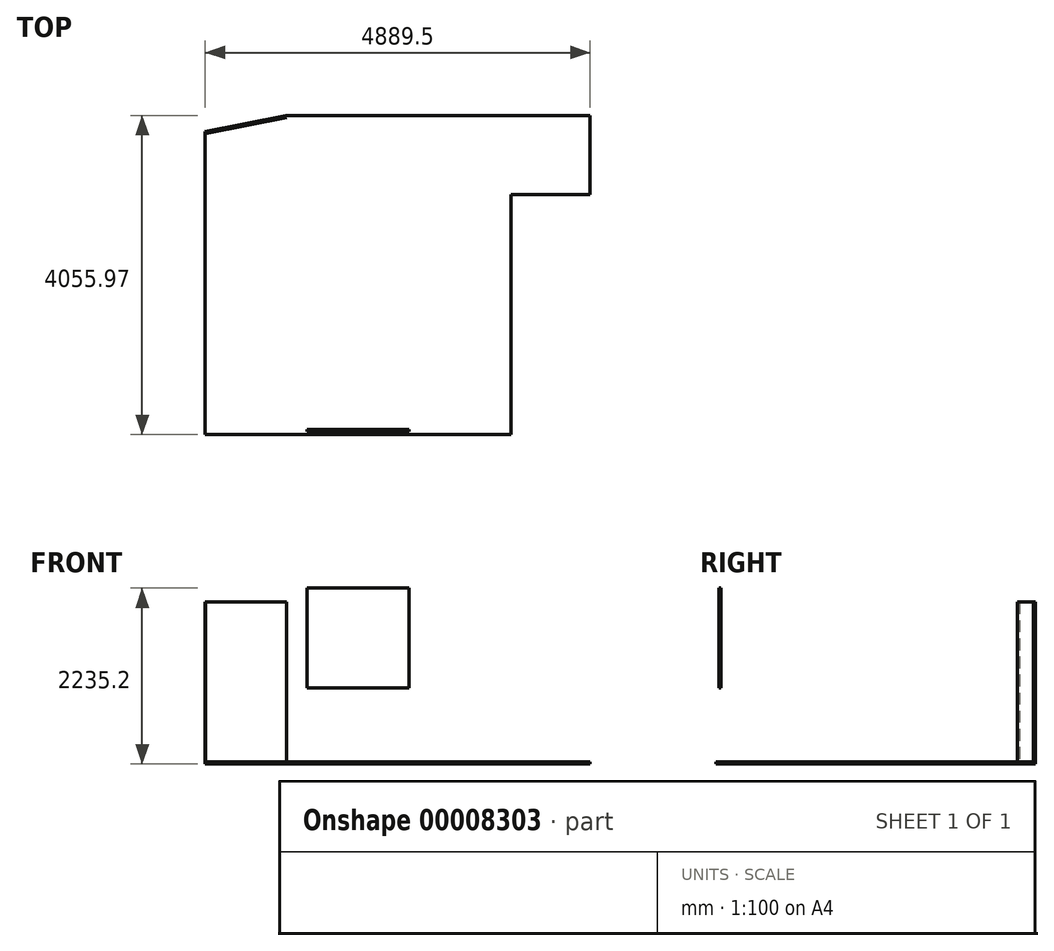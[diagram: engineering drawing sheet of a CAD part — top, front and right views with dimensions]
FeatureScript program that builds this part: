
annotation { "Feature Type Name" : "Feature", "Feature Type Description" : "" }
export const myFeature = defineFeature(function(context is Context, id is Id, definition is map)
    precondition{}
    {
        {
            var Q0;
            Q0=qCreatedBy(makeId("Top.planeOp"),FACE);
            var sketch = newSketch(context, id + "F0", { "sketchPlane" : qUnion([Q0])});
            skLineSegment(sketch, "E0", {"start": v(-541.3, 4018.52) * mm, "end": v(3319.5, 4018.52) * mm});
            skLineSegment(sketch, "E1", {"start": v(3319.5, 4018.52) * mm, "end": v(3319.5, 3015.22) * mm});
            skLineSegment(sketch, "E2", {"start": v(3319.5, 3015.22) * mm, "end": v(2316.2, 3015.22) * mm});
            skLineSegment(sketch, "E3", {"start": v(2316.2, 3015.22) * mm, "end": v(2316.2, -32.78) * mm});
            skLineSegment(sketch, "E4", {"start": v(2316.2, -32.78) * mm, "end": v(1020.8, -32.78) * mm});
            skLineSegment(sketch, "E5", {"start": v(1020.8, -32.78) * mm, "end": v(1020.8, -37.45) * mm});
            skLineSegment(sketch, "E6", {"start": v(1020.8, -37.45) * mm, "end": v(-274.6, -37.45) * mm});
            skLineSegment(sketch, "E7", {"start": v(-274.6, -37.45) * mm, "end": v(-274.6, -32.78) * mm});
            skLineSegment(sketch, "E8", {"start": v(-274.6, -32.78) * mm, "end": v(-1570, -32.78) * mm});
            skLineSegment(sketch, "E9", {"start": v(-1570, -32.78) * mm, "end": v(-1570, 3815.32) * mm});
            skLineSegment(sketch, "E10", {"start": v(-1570, 3815.32) * mm, "end": v(-541.3, 4018.52) * mm});
            skSolve(sketch);
        }
        {
            var Q0;
            Q0 = qSketchRegion(id + "F0", true);
            extrude(context, id + "F1", {"entities" : qUnion([Q0]), "oppositeDirection" : true, "depth" : 25.4 * mm});
        }
        {
            var Q0;
            Q0=qCreatedBy(makeId("Front.planeOp"),FACE);
            var sketch = newSketch(context, id + "F2", { "sketchPlane" : qUnion([Q0])});
            skLineSegment(sketch, "E11.bottom", {"start": v(-274.6, 939.8) * mm, "end": v(1020.8, 939.8) * mm});
            skLineSegment(sketch, "E11.top", {"start": v(-274.6, 2209.8) * mm, "end": v(1020.8, 2209.8) * mm});
            skLineSegment(sketch, "E11.left", {"start": v(-274.6, 939.8) * mm, "end": v(-274.6, 2209.8) * mm});
            skLineSegment(sketch, "E11.right", {"start": v(1020.8, 939.8) * mm, "end": v(1020.8, 2209.8) * mm});
            skSolve(sketch);
        }
        {
            var Q0;
            Q0 = qSketchRegion(id + "F2", true);
            extrude(context, id + "F3", {"entities" : qUnion([Q0]), "oppositeDirection" : true, "depth" : 25.4 * mm});
        }
        {
            var Q0;
            Q0=qCreatedBy(makeId("Top.planeOp"),FACE);
            var sketch = newSketch(context, id + "F4", { "sketchPlane" : qUnion([Q0])});
            skLineSegment(sketch, "E12.bottom", {"start": v(-1565.08, 3790.4) * mm, "end": v(-536.38, 3993.6) * mm});
            skLineSegment(sketch, "E12.top", {"start": v(-1570, 3815.32) * mm, "end": v(-541.3, 4018.52) * mm});
            skLineSegment(sketch, "E12.left", {"start": v(-1570, 3815.32) * mm, "end": v(-1565.08, 3790.4) * mm});
            skLineSegment(sketch, "E12.right", {"start": v(-541.3, 4018.52) * mm, "end": v(-536.38, 3993.6) * mm});
            skSolve(sketch);
        }
        {
            var Q0;
            Q0 = qSketchRegion(id + "F4", true);
            extrude(context, id + "F5", {"entities" : qUnion([Q0]), "depth" : 2032 * mm});
        }
    });
